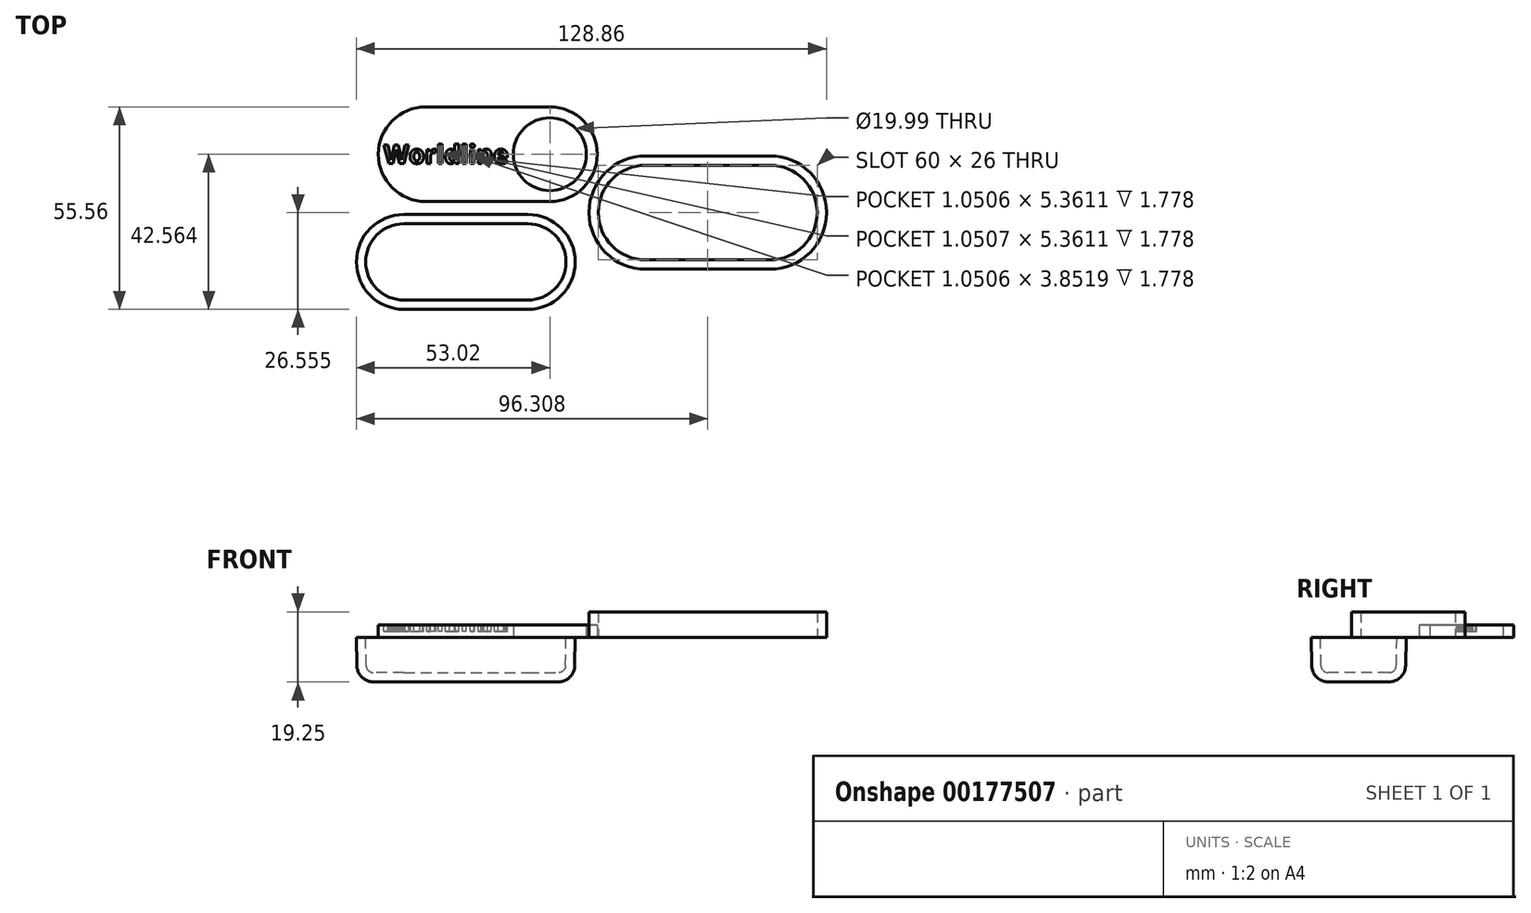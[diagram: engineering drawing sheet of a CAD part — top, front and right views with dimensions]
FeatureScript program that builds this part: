
annotation { "Feature Type Name" : "Feature", "Feature Type Description" : "" }
export const myFeature = defineFeature(function(context is Context, id is Id, definition is map)
    precondition{}
    {
        {
            var Q0;
            Q0=qCreatedBy(makeId("Top.planeOp"),FACE);
            var sketch = newSketch(context, id + "F0", { "sketchPlane" : qUnion([Q0])});
            skLineSegment(sketch, "E0.bottom", {"start": v(0, 0) * mm, "end": v(-60, 0) * mm});
            skLineSegment(sketch, "E0.top", {"start": v(0, -26) * mm, "end": v(-60, -26) * mm});
            skLineSegment(sketch, "E0.left", {"start": v(0, 0) * mm, "end": v(0, -26) * mm});
            skLineSegment(sketch, "E0.right", {"start": v(-60, 0) * mm, "end": v(-60, -26) * mm});
            skCircle(sketch, "E1", {"center": v(-47, -13) * mm, "radius": 13 * mm});
            skCircle(sketch, "E2", {"center": v(-13, -13) * mm, "radius": 13 * mm});
            skSolve(sketch);
        }
        {
            var Q0;
            {var subQ0=sQuery(id+"F0.wireOp",EDGE,"E1");var subQ1=makeQuery(id+"F0.imprint","INTERSECT",VERTEX,{"derivedFrom":[sQuery(id+"F0.wireOp",EDGE,"E0.bottom"),subQ0]});Q0=makeQuery(id+"F0.imprint","IMPRINT",FACE,{"disambiguationData":[TD([[makeQuery(id+"F0.imprint","IMPRINT",EDGE,{"disambiguationData":[TD([[subQ1,-1.0]])],"derivedFrom":subQ0}),1.0]])]});}
            var Q1;
            {var subQ0=sQuery(id+"F0.wireOp",EDGE,"E2");var subQ1=sQuery(id+"F0.wireOp",EDGE,"E0.bottom");var subQ2=makeQuery(id+"F0.imprint","INTERSECT",VERTEX,{"derivedFrom":[subQ1,subQ0]});Q1=makeQuery(id+"F0.imprint","IMPRINT",FACE,{"disambiguationData":[TD([[makeQuery(id+"F0.imprint","IMPRINT",EDGE,{"disambiguationData":[TD([[subQ2,-1.0]])],"derivedFrom":subQ1}),1.0]])]});}
            var Q2;
            {var subQ0=sQuery(id+"F0.wireOp",EDGE,"E2");var subQ1=makeQuery(id+"F0.imprint","INTERSECT",VERTEX,{"derivedFrom":[sQuery(id+"F0.wireOp",EDGE,"E0.bottom"),subQ0]});Q2=makeQuery(id+"F0.imprint","IMPRINT",FACE,{"disambiguationData":[TD([[makeQuery(id+"F0.imprint","IMPRINT",EDGE,{"disambiguationData":[TD([[subQ1,1.0]])],"derivedFrom":subQ0}),1.0]])]});}
            extrude(context, id + "F1", {"entities" : qUnion([Q0, Q1, Q2]), "oppositeDirection" : true, "depth" : 12.2 * mm, "hasDraft" : true, "draftAngle" : 1 * degree, "draftPullDirection" : true});
        }
        {
            var Q0;
            Q0=makeQuery(id+"F1.opExtrude","CAP_FACE",FACE,{"disambiguationData":[OSD([sQuery(id+"F0.wireOp",EDGE,"E0.bottom"),sQuery(id+"F0.wireOp",EDGE,"E0.top"),sQuery(id+"F0.wireOp",EDGE,"E1"),sQuery(id+"F0.wireOp",EDGE,"E2")])],"isStart":false});
            fillet(context, id + "F2", {"entities" : qUnion([Q0]), "radius" : 4.57 * mm, "tangentPropagation" : true, "allowEdgeOverflow" : false});
        }
        {
            var Q0;
            Q0=qCreatedBy(makeId("Top.planeOp"),FACE);
            var sketch = newSketch(context, id + "F3", { "sketchPlane" : qUnion([Q0])});
            skLineSegment(sketch, "E3.bottom", {"start": v(6.02, 29.56) * mm, "end": v(-53.98, 29.56) * mm});
            skLineSegment(sketch, "E3.top", {"start": v(6.02, 3.56) * mm, "end": v(-53.98, 3.56) * mm});
            skLineSegment(sketch, "E3.left", {"start": v(6.02, 29.56) * mm, "end": v(6.02, 3.56) * mm});
            skLineSegment(sketch, "E3.right", {"start": v(-53.98, 29.56) * mm, "end": v(-53.98, 3.56) * mm});
            skCircle(sketch, "E4", {"center": v(-40.98, 16.56) * mm, "radius": 13 * mm});
            skCircle(sketch, "E5", {"center": v(-6.98, 16.56) * mm, "radius": 13 * mm});
            skCircle(sketch, "E6", {"center": v(-41.18, 16.56) * mm, "radius": 10 * mm});
            skPoint(sketch, "E7", {"position": v(-53.98, 16.56) * mm});
            skLineSegment(sketch, "E8", {"start": v(-53.98, 16.56) * mm, "end": v(-51.18, 16.56) * mm, "construction": true});
            skCircle(sketch, "E9", {"center": v(-6.98, 16.56) * mm, "radius": 10 * mm});
            skSolve(sketch);
        }
        {
            var Q0;
            {var subQ0=sQuery(id+"F3.wireOp",EDGE,"E5");var subQ1=makeQuery(id+"F3.imprint","INTERSECT",VERTEX,{"derivedFrom":[sQuery(id+"F3.wireOp",EDGE,"E3.bottom"),subQ0]});Q0=makeQuery(id+"F3.imprint","IMPRINT",FACE,{"disambiguationData":[TD([[makeQuery(id+"F3.imprint","IMPRINT",EDGE,{"disambiguationData":[TD([[subQ1,1.0]])],"derivedFrom":subQ0}),1.0]])]});}
            var Q1;
            {var subQ0=sQuery(id+"F3.wireOp",EDGE,"E5");var subQ1=sQuery(id+"F3.wireOp",EDGE,"E3.bottom");var subQ2=makeQuery(id+"F3.imprint","INTERSECT",VERTEX,{"derivedFrom":[subQ1,subQ0]});Q1=makeQuery(id+"F3.imprint","IMPRINT",FACE,{"disambiguationData":[TD([[makeQuery(id+"F3.imprint","IMPRINT",EDGE,{"disambiguationData":[TD([[subQ2,-1.0]])],"derivedFrom":subQ1}),1.0]])]});}
            var Q2;
            Q2=makeQuery(id+"F3.imprint","IMPRINT",FACE,{"disambiguationData":[TD([[makeQuery(id+"F3.imprint","IMPRINT",EDGE,{"derivedFrom":sQuery(id+"F3.wireOp",EDGE,"a6fba586-438c-4d96-be7d-434e70076c33.sketch_text.stroke-20")}),1.0]])]});
            var Q3;
            Q3=makeQuery(id+"F3.imprint","IMPRINT",FACE,{"disambiguationData":[TD([[makeQuery(id+"F3.imprint","IMPRINT",EDGE,{"derivedFrom":sQuery(id+"F3.wireOp",EDGE,"a6fba586-438c-4d96-be7d-434e70076c33.sketch_text.stroke-0")}),1.0]])]});
            var Q4;
            Q4=makeQuery(id+"F3.imprint","IMPRINT",FACE,{"disambiguationData":[TD([[makeQuery(id+"F3.imprint","IMPRINT",EDGE,{"derivedFrom":sQuery(id+"F3.wireOp",EDGE,"E6")}),-1.0]])]});
            var Q5;
            Q5=makeQuery(id+"F3.imprint","IMPRINT",FACE,{"disambiguationData":[TD([[makeQuery(id+"F3.imprint","IMPRINT",EDGE,{"derivedFrom":sQuery(id+"F3.wireOp",EDGE,"f5b48d19-ef08-4ac2-a32c-5731788e0d77.sketch_text.stroke-82")}),1.0]])]});
            var Q6;
            {var subQ0=sQuery(id+"F3.wireOp",EDGE,"f5b48d19-ef08-4ac2-a32c-5731788e0d77.sketch_text.stroke-125");Q6=makeQuery(id+"F3.imprint","IMPRINT",FACE,{"disambiguationData":[TD([[makeQuery(id+"F3.imprint","IMPRINT",EDGE,{"derivedFrom":subQ0}),1.0]])]});}
            var Q7;
            Q7=makeQuery(id+"F3.imprint","IMPRINT",FACE,{"disambiguationData":[TD([[makeQuery(id+"F3.imprint","IMPRINT",EDGE,{"derivedFrom":sQuery(id+"F3.wireOp",EDGE,"f5b48d19-ef08-4ac2-a32c-5731788e0d77.sketch_text.stroke-0")}),1.0]])]});
            var Q8;
            {var subQ5=sQuery(id+"F3.wireOp",EDGE,"f5b48d19-ef08-4ac2-a32c-5731788e0d77.sketch_text.stroke-86");Q8=makeQuery(id+"F3.imprint","IMPRINT",FACE,{"disambiguationData":[TD([[makeQuery(id+"F3.imprint","IMPRINT",EDGE,{"derivedFrom":subQ5}),-1.0]])]});}
            var Q9;
            {var subQ5=sQuery(id+"F3.wireOp",EDGE,"f5b48d19-ef08-4ac2-a32c-5731788e0d77.sketch_text.stroke-88");Q9=makeQuery(id+"F3.imprint","IMPRINT",FACE,{"disambiguationData":[TD([[makeQuery(id+"F3.imprint","IMPRINT",EDGE,{"derivedFrom":subQ5}),-1.0]])]});}
            var Q10;
            Q10=makeQuery(id+"F3.imprint","IMPRINT",FACE,{"disambiguationData":[TD([[makeQuery(id+"F3.imprint","IMPRINT",EDGE,{"derivedFrom":sQuery(id+"F3.wireOp",EDGE,"E6")}),1.0]])]});
            extrude(context, id + "F4", {"entities" : qUnion([Q0, Q1, Q2, Q3, Q4, Q5, Q6, Q7, Q8, Q9, Q10]), "depth" : 3.4 * mm});
        }
        {
            var Q0;
            Q0=makeQuery(id+"F1.opExtrude","CAP_FACE",FACE,{"disambiguationData":[OSD([sQuery(id+"F0.wireOp",EDGE,"E0.bottom"),sQuery(id+"F0.wireOp",EDGE,"E0.top"),sQuery(id+"F0.wireOp",EDGE,"E1"),sQuery(id+"F0.wireOp",EDGE,"E2")])],"isStart":true});
            shell(context, id + "F5", {"entities" : qUnion([Q0]), "thickness" : 2.54 * mm});
        }
        {
            var Q0;
            Q0=qCreatedBy(makeId("Top.planeOp"),FACE);
            var sketch = newSketch(context, id + "F6", { "sketchPlane" : qUnion([Q0])});
            skLineSegment(sketch, "E10.bottom", {"start": v(53.3, 13.56) * mm, "end": v(19.3, 13.56) * mm});
            skLineSegment(sketch, "E10.top", {"start": v(53.3, -12.44) * mm, "end": v(19.3, -12.44) * mm});
            skArc(sketch, "E11", {"start": v(19.3, 13.56) * mm, "mid": v(6.3, 0.56) * mm, "end": v(19.3, -12.44) * mm});
            skArc(sketch, "E12", {"start": v(53.3, -12.44) * mm, "mid": v(66.3, 0.56) * mm, "end": v(53.3, 13.56) * mm});
            skLineSegment(sketch, "E13.0", {"start": v(53.3, 16.1) * mm, "end": v(19.3, 16.1) * mm});
            skArc(sketch, "E13.1", {"start": v(53.3, -15) * mm, "mid": v(68.86, 0.56) * mm, "end": v(53.3, 16.1) * mm});
            skLineSegment(sketch, "E13.2", {"start": v(53.3, -15) * mm, "end": v(19.3, -15) * mm});
            skArc(sketch, "E13.3", {"start": v(19.3, 16.1) * mm, "mid": v(3.76, 0.56) * mm, "end": v(19.3, -15) * mm});
            skSolve(sketch);
        }
        {
            var Q0;
            Q0=makeQuery(id+"F6.imprint","IMPRINT",FACE,{"disambiguationData":[TD([[makeQuery(id+"F6.imprint","IMPRINT",EDGE,{"derivedFrom":sQuery(id+"F6.wireOp",EDGE,"E10.bottom")}),-1.0]])]});
            extrude(context, id + "F7", {"entities" : qUnion([Q0]), "depth" : 7.05 * mm});
        }
        {
            var Q0;
            Q0=makeQuery(id+"F4.opExtrude","CAP_FACE",FACE,{"disambiguationData":[OSD([sQuery(id+"F3.wireOp",EDGE,"E3.bottom"),sQuery(id+"F3.wireOp",EDGE,"E3.top"),sQuery(id+"F3.wireOp",EDGE,"E4"),sQuery(id+"F3.wireOp",EDGE,"E5"),sQuery(id+"F3.wireOp",EDGE,"E9")])],"isStart":false});
            var sketch = newSketch(context, id + "F8", { "sketchPlane" : qUnion([Q0])});
            skText(sketch, "E14", { "text": "Worldline", "fontName": "OpenSans-Bold.ttf"});
            const initialGuessF8  = {"E14": [-0.05246, 0.01402, 1, 0, 0.00508]};
            skSetInitialGuess(sketch, initialGuessF8);
            skSolve(sketch);
        }
        {
            var Q0;
            Q0 = qSketchRegion(id + "F8", true);
            extrude(context, id + "F9", {"entities" : qUnion([Q0]), "operationType" : NewBodyOperationType.REMOVE, "oppositeDirection" : true, "depth" : 1.78 * mm});
        }
    });
